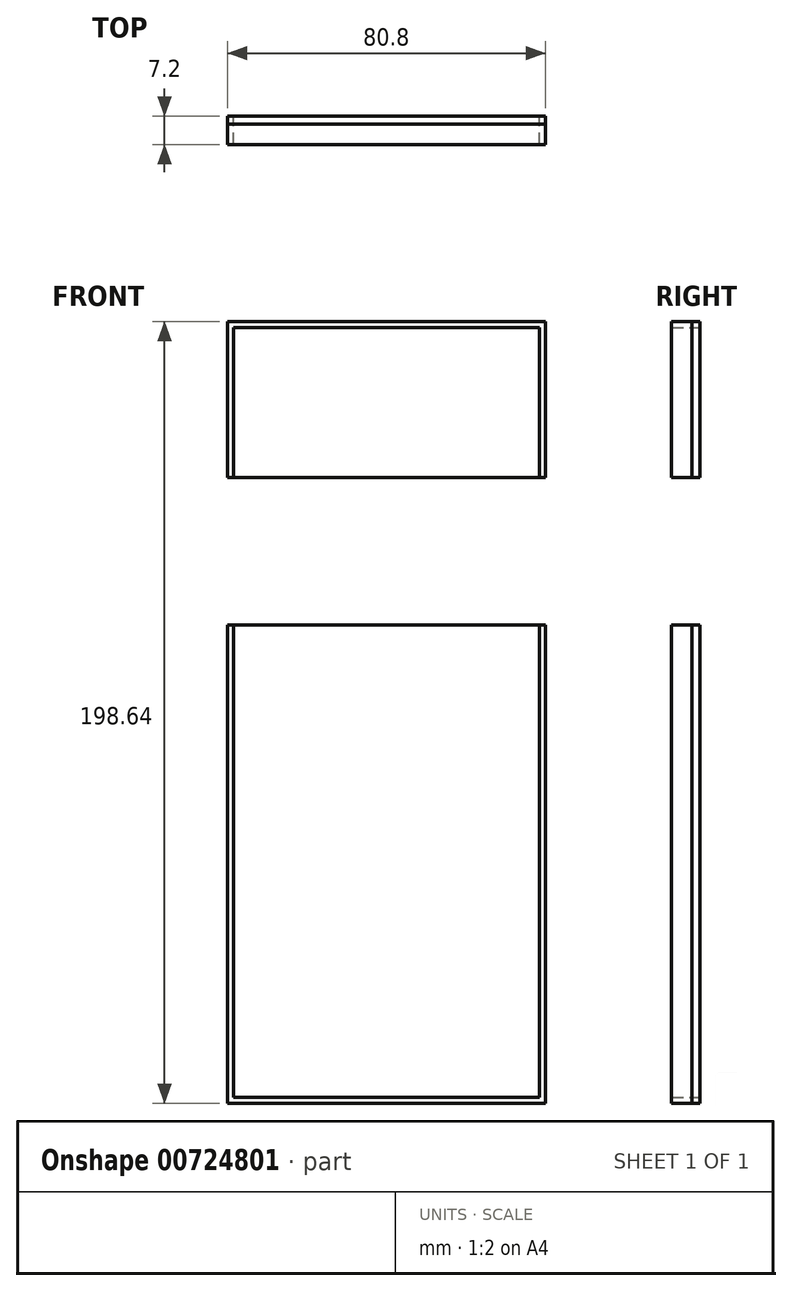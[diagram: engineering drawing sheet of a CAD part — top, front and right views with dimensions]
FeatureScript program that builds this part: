
annotation { "Feature Type Name" : "Feature", "Feature Type Description" : "" }
export const myFeature = defineFeature(function(context is Context, id is Id, definition is map)
    precondition{}
    {
        {
            var Q0;
            Q0=qCreatedBy(makeId("Front.planeOp"),FACE);
            var sketch = newSketch(context, id + "F0", { "sketchPlane" : qUnion([Q0])});
            skLineSegment(sketch, "E0.bottom", {"start": v(38.9, -60) * mm, "end": v(-38.9, -60) * mm});
            skLineSegment(sketch, "E0.top", {"start": v(38.9, 60) * mm, "end": v(-38.9, 60) * mm});
            skLineSegment(sketch, "E0.left", {"start": v(38.9, -60) * mm, "end": v(38.9, 60) * mm});
            skLineSegment(sketch, "E0.right", {"start": v(-38.9, -60) * mm, "end": v(-38.9, 60) * mm});
            skPoint(sketch, "E0.middle", {"position": v(0, 0) * mm});
            skLineSegment(sketch, "E1.bottom", {"start": v(38.9, 97.54) * mm, "end": v(-38.9, 97.54) * mm});
            skLineSegment(sketch, "E1.top", {"start": v(38.9, 135.64) * mm, "end": v(-38.9, 135.64) * mm});
            skLineSegment(sketch, "E1.left", {"start": v(38.9, 97.54) * mm, "end": v(38.9, 135.64) * mm});
            skLineSegment(sketch, "E1.right", {"start": v(-38.9, 97.54) * mm, "end": v(-38.9, 135.64) * mm});
            skPoint(sketch, "E1.middle", {"position": v(0, 117.34) * mm});
            skLineSegment(sketch, "E2", {"start": v(-38.9, 60) * mm, "end": v(-40.4, 60) * mm});
            skLineSegment(sketch, "E3.bottom", {"start": v(40.4, -61.5) * mm, "end": v(-40.4, -61.5) * mm});
            skLineSegment(sketch, "E3.top", {"start": v(40.4, 60) * mm, "end": v(-40.4, 60) * mm});
            skLineSegment(sketch, "E3.left", {"start": v(40.4, -61.5) * mm, "end": v(40.4, 60) * mm});
            skLineSegment(sketch, "E3.right", {"start": v(-40.4, -61.5) * mm, "end": v(-40.4, 60) * mm});
            skPoint(sketch, "E3.middle", {"position": v(0, -0.75) * mm});
            skLineSegment(sketch, "E4.bottom", {"start": v(40.4, 97.54) * mm, "end": v(-40.4, 97.54) * mm});
            skLineSegment(sketch, "E4.top", {"start": v(40.4, 137.14) * mm, "end": v(-40.4, 137.14) * mm});
            skLineSegment(sketch, "E4.left", {"start": v(40.4, 97.54) * mm, "end": v(40.4, 137.14) * mm});
            skLineSegment(sketch, "E4.right", {"start": v(-40.4, 97.54) * mm, "end": v(-40.4, 137.14) * mm});
            skSolve(sketch);
        }
        {
            var Q0;
            Q0=makeQuery(id+"F0.imprint","IMPRINT",FACE,{"disambiguationData":[TD([[makeQuery(id+"F0.imprint","IMPRINT",EDGE,{"derivedFrom":sQuery(id+"F0.wireOp",EDGE,"E1.top")}),-1.0]])]});
            var Q1;
            Q1=makeQuery(id+"F0.imprint","IMPRINT",FACE,{"disambiguationData":[TD([[makeQuery(id+"F0.imprint","IMPRINT",EDGE,{"derivedFrom":sQuery(id+"F0.wireOp",EDGE,"E0.bottom")}),1.0]])]});
            extrude(context, id + "F1", {"entities" : qUnion([Q0, Q1]), "depth" : 7.2 * mm, "offsetDistance" : 25 * mm});
        }
        {
            var Q0;
            Q0=qSketchRegion(id+"F0",true);
            extrude(context, id + "F2", {"entities" : qUnion([Q0]), "depth" : 2 * mm, "offsetDistance" : 25 * mm});
        }
    });
